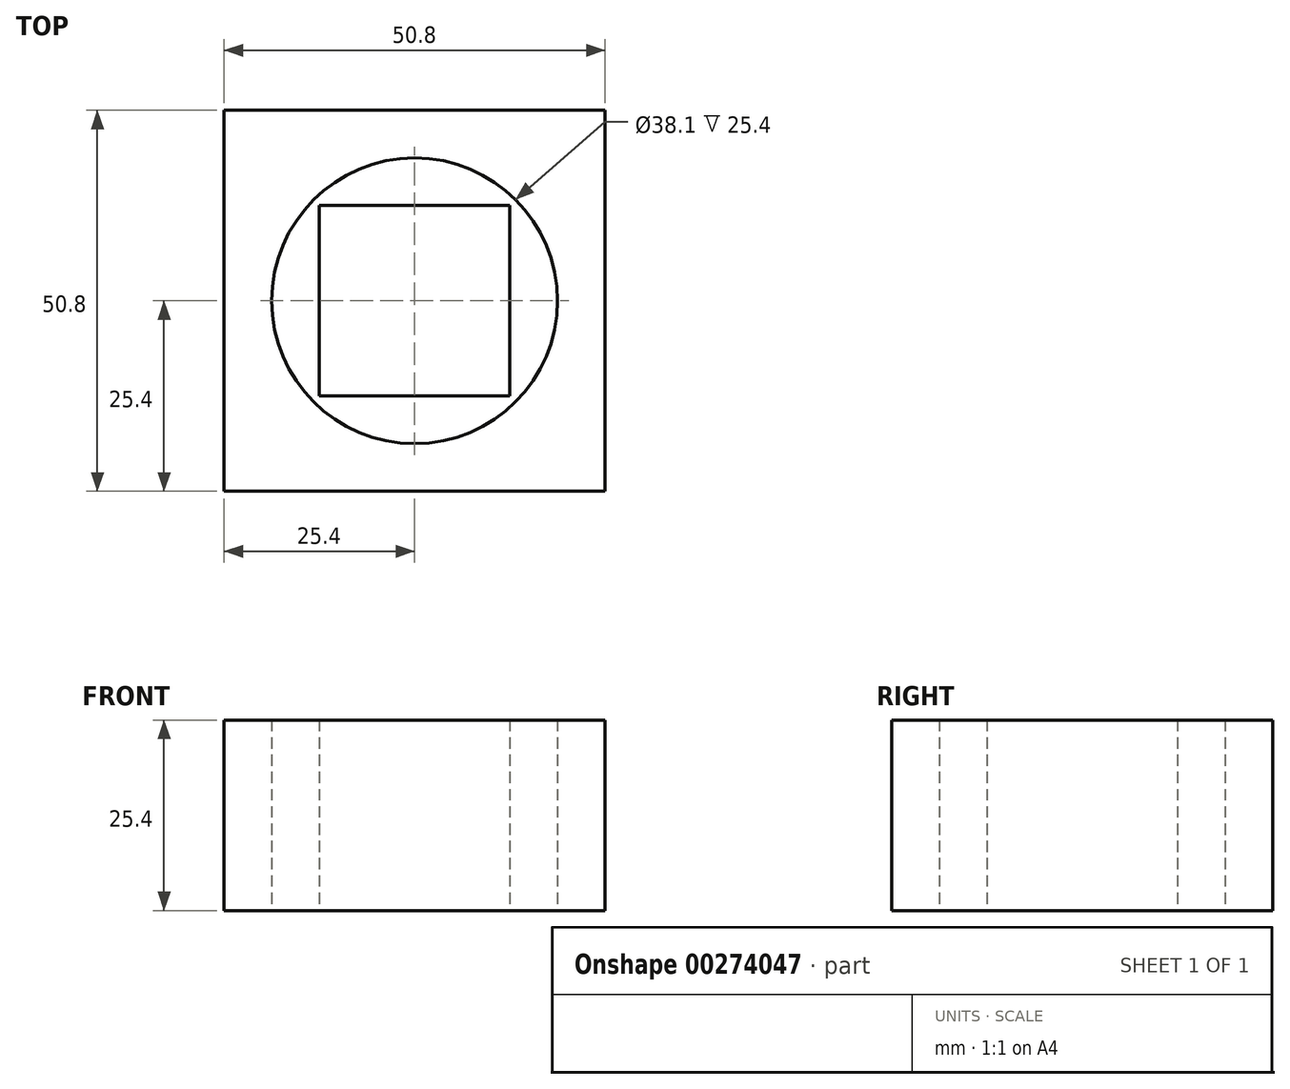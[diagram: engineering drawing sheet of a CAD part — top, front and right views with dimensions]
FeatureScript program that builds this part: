
annotation { "Feature Type Name" : "Feature", "Feature Type Description" : "" }
export const myFeature = defineFeature(function(context is Context, id is Id, definition is map)
    precondition{}
    {
        {
            var Q0;
            Q0=qCreatedBy(makeId("Top.planeOp"),FACE);
            var sketch = newSketch(context, id + "F0", { "sketchPlane" : qUnion([Q0])});
            skLineSegment(sketch, "E0.bottom", {"start": v(0, 0) * mm, "end": v(50.8, 0) * mm});
            skLineSegment(sketch, "E0.top", {"start": v(0, 50.8) * mm, "end": v(50.8, 50.8) * mm});
            skLineSegment(sketch, "E0.left", {"start": v(0, 0) * mm, "end": v(0, 50.8) * mm});
            skLineSegment(sketch, "E0.right", {"start": v(50.8, 0) * mm, "end": v(50.8, 50.8) * mm});
            skCircle(sketch, "E1", {"center": v(25.4, 25.4) * mm, "radius": 19.05 * mm});
            skPoint(sketch, "E1.centerSnap0", {"position": v(0, 25.4) * mm});
            skPoint(sketch, "E1.centerSnap1", {"position": v(25.4, 0) * mm});
            skLineSegment(sketch, "E2.bottom", {"start": v(38.1, 12.7) * mm, "end": v(12.7, 12.7) * mm});
            skLineSegment(sketch, "E2.top", {"start": v(38.1, 38.1) * mm, "end": v(12.7, 38.1) * mm});
            skLineSegment(sketch, "E2.left", {"start": v(38.1, 12.7) * mm, "end": v(38.1, 38.1) * mm});
            skLineSegment(sketch, "E2.right", {"start": v(12.7, 12.7) * mm, "end": v(12.7, 38.1) * mm});
            skSolve(sketch);
        }
        {
            var Q0;
            Q0=makeQuery(id+"F0.imprint","IMPRINT",FACE,{"disambiguationData":[TD([[makeQuery(id+"F0.imprint","IMPRINT",EDGE,{"derivedFrom":sQuery(id+"F0.wireOp",EDGE,"E0.bottom")}),1.0]])]});
            var Q1;
            Q1=makeQuery(id+"F0.imprint","IMPRINT",FACE,{"disambiguationData":[TD([[makeQuery(id+"F0.imprint","IMPRINT",EDGE,{"derivedFrom":sQuery(id+"F0.wireOp",EDGE,"E2.bottom")}),-1.0]])]});
            extrude(context, id + "F1", {"entities" : qUnion([Q0, Q1]), "depth" : 25.4 * mm});
        }
    });
